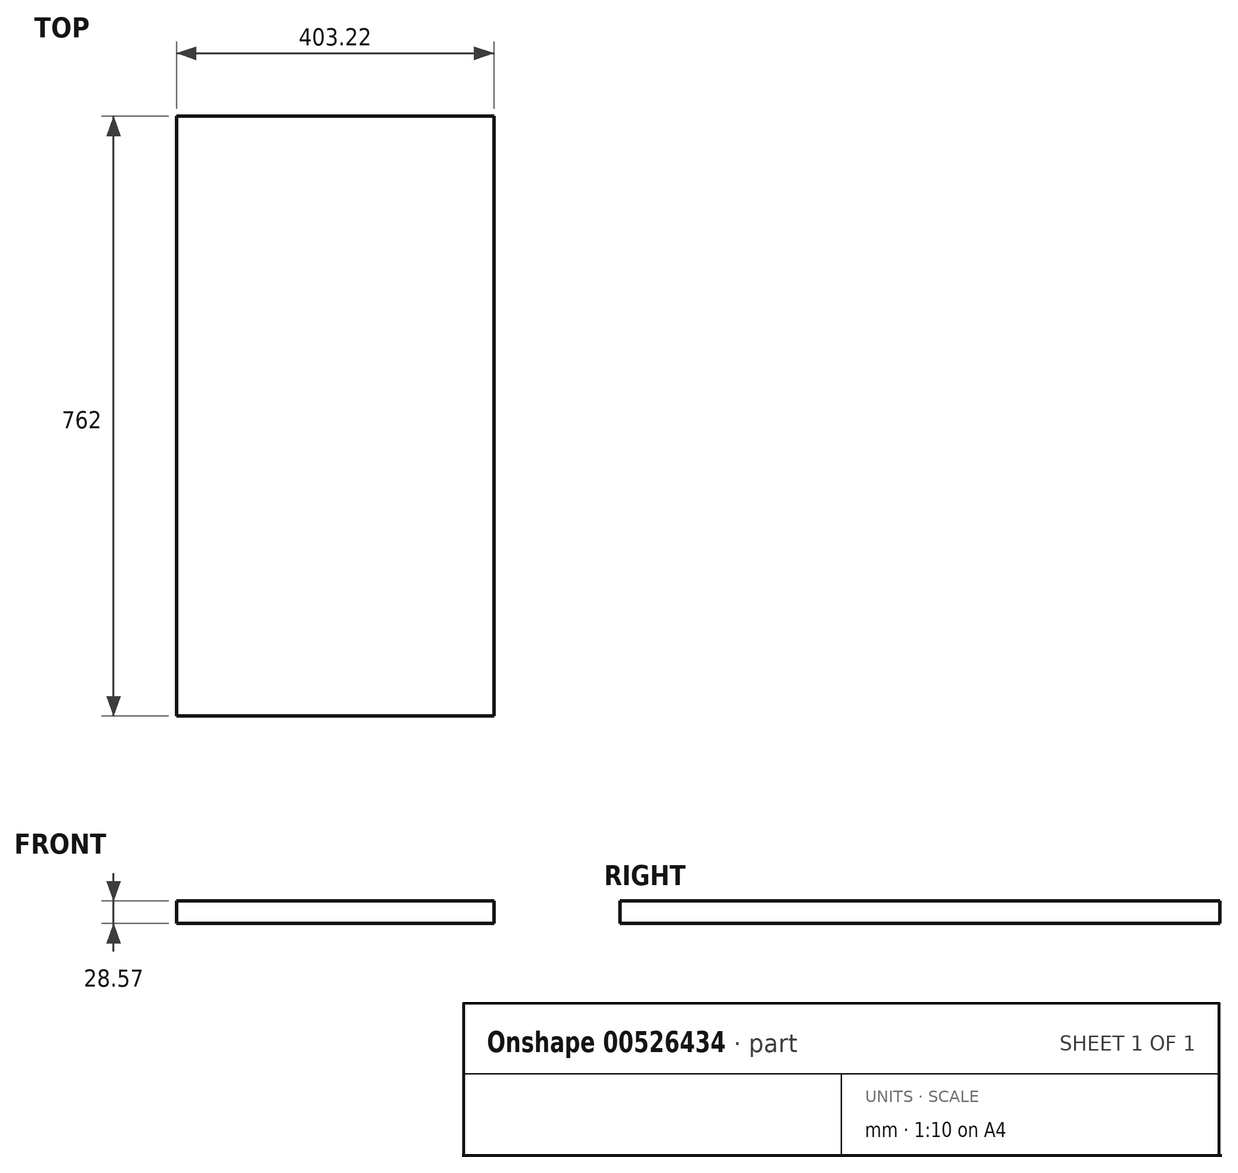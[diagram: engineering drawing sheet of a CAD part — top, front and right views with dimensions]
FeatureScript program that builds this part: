
annotation { "Feature Type Name" : "Feature", "Feature Type Description" : "" }
export const myFeature = defineFeature(function(context is Context, id is Id, definition is map)
    precondition{}
    {
        {
            var Q0;
            Q0=qCreatedBy(makeId("Top.planeOp"),FACE);
            var sketch = newSketch(context, id + "F0", { "sketchPlane" : qUnion([Q0])});
            skLineSegment(sketch, "E0.bottom", {"start": v(201.61, 381) * mm, "end": v(-201.61, 381) * mm});
            skLineSegment(sketch, "E0.top", {"start": v(201.61, -381) * mm, "end": v(-201.61, -381) * mm});
            skLineSegment(sketch, "E0.left", {"start": v(201.61, 381) * mm, "end": v(201.61, -381) * mm});
            skLineSegment(sketch, "E0.right", {"start": v(-201.61, 381) * mm, "end": v(-201.61, -381) * mm});
            skPoint(sketch, "E0.middle", {"position": v(0, 0) * mm});
            skSolve(sketch);
        }
        {
            var Q0;
            Q0=makeQuery(id+"F0.imprint","IMPRINT",FACE,{"disambiguationData":[TD([[makeQuery(id+"F0.imprint","IMPRINT",EDGE,{"derivedFrom":sQuery(id+"F0.wireOp",EDGE,"E0.bottom")}),1.0]])]});
            extrude(context, id + "F1", {"entities" : qUnion([Q0]), "depth" : 28.57 * mm, "offsetDistance" : 25.4 * mm});
        }
    });
